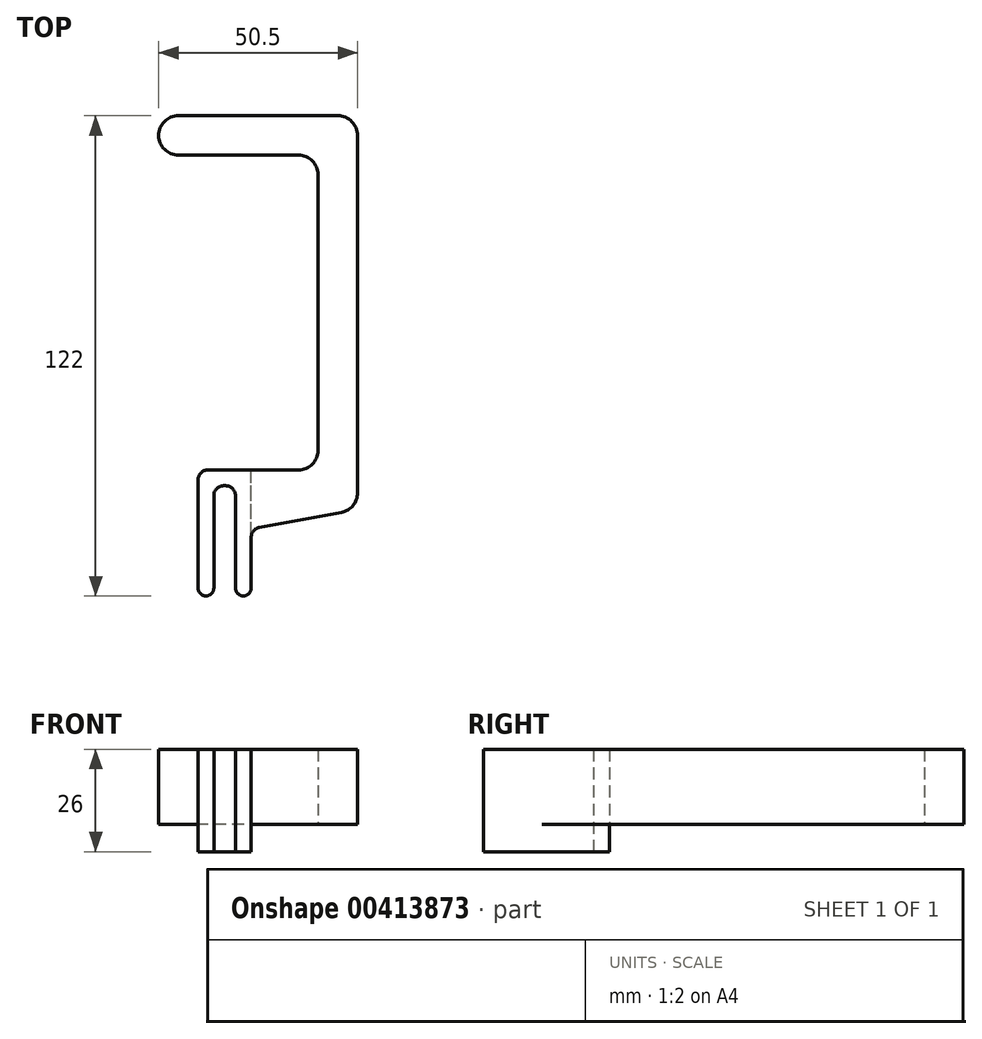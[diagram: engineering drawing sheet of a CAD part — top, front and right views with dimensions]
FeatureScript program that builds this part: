
annotation { "Feature Type Name" : "Feature", "Feature Type Description" : "" }
export const myFeature = defineFeature(function(context is Context, id is Id, definition is map)
    precondition{}
    {
        {
            var Q0;
            Q0=qCreatedBy(makeId("Top.planeOp"),FACE);
            var sketch = newSketch(context, id + "F0", { "sketchPlane" : qUnion([Q0])});
            skLineSegment(sketch, "E0", {"start": v(0, 0) * mm, "end": v(0, 30) * mm});
            skLineSegment(sketch, "E1", {"start": v(0, 0) * mm, "end": v(4, 0) * mm});
            skLineSegment(sketch, "E2", {"start": v(4, 0) * mm, "end": v(4, 26) * mm});
            skLineSegment(sketch, "E3", {"start": v(4, 26) * mm, "end": v(9.5, 26) * mm});
            skLineSegment(sketch, "E4", {"start": v(9.5, 26) * mm, "end": v(9.5, 0) * mm});
            skLineSegment(sketch, "E5", {"start": v(0, 30) * mm, "end": v(30.5, 30) * mm});
            skLineSegment(sketch, "E6", {"start": v(30.5, 30) * mm, "end": v(30.5, 110) * mm});
            skLineSegment(sketch, "E7", {"start": v(30.5, 120) * mm, "end": v(40.5, 120) * mm});
            skLineSegment(sketch, "E8", {"start": v(40.5, 120) * mm, "end": v(40.5, 20) * mm});
            skArc(sketch, "E9", {"start": v(0, 0) * mm, "mid": v(2, -2) * mm, "end": v(4, 0) * mm});
            skLineSegment(sketch, "E10", {"start": v(9.5, 0) * mm, "end": v(13.5, 0) * mm});
            skLineSegment(sketch, "E11", {"start": v(13.5, 0) * mm, "end": v(13.5, 15) * mm});
            skArc(sketch, "E12", {"start": v(9.5, 0) * mm, "mid": v(11.5, -2) * mm, "end": v(13.5, 0) * mm});
            skLineSegment(sketch, "E13.bottom", {"start": v(30.5, 120) * mm, "end": v(-5, 120) * mm});
            skLineSegment(sketch, "E13.top", {"start": v(30.5, 110) * mm, "end": v(-5, 110) * mm});
            skLineSegment(sketch, "E13.right", {"start": v(-5, 120) * mm, "end": v(-5, 110) * mm});
            skArc(sketch, "E14", {"start": v(-5, 120) * mm, "mid": v(-10, 115) * mm, "end": v(-5, 110) * mm});
            skLineSegment(sketch, "E15", {"start": v(13.5, 15) * mm, "end": v(40.5, 20) * mm});
            skPoint(sketch, "E16.end.orphan", {"position": v(40.5, 15) * mm});
            skSolve(sketch);
        }
        {
            var Q0;
            Q0 = qSketchRegion(id + "F0", true);
            extrude(context, id + "F1", {"entities" : qUnion([Q0]), "depth" : 26 * mm});
        }
        {
            var Q0;
            Q0=makeQuery(id+"F1.opExtrude","CAP_FACE",FACE,{"disambiguationData":[OSD([sQuery(id+"F0.wireOp",EDGE,"E0"),sQuery(id+"F0.wireOp",EDGE,"E2"),sQuery(id+"F0.wireOp",EDGE,"E3"),sQuery(id+"F0.wireOp",EDGE,"E4"),sQuery(id+"F0.wireOp",EDGE,"E5"),sQuery(id+"F0.wireOp",EDGE,"E6"),sQuery(id+"F0.wireOp",EDGE,"E7"),sQuery(id+"F0.wireOp",EDGE,"E8"),sQuery(id+"F0.wireOp",EDGE,"E9"),sQuery(id+"F0.wireOp",EDGE,"E11"),sQuery(id+"F0.wireOp",EDGE,"E12"),sQuery(id+"F0.wireOp",EDGE,"E16")])],"isStart":true});
            var sketch = newSketch(context, id + "F2", { "sketchPlane" : qUnion([Q0])});
            skLineSegment(sketch, "E17.0", {"start": v(40.5, -120) * mm, "end": v(40.5, -120) * mm});
            skLineSegment(sketch, "E17.1", {"start": v(40.5, -120) * mm, "end": v(40.5, -120) * mm});
            skLineSegment(sketch, "E17.2", {"start": v(30.5, -30) * mm, "end": v(30.5, -110) * mm});
            skLineSegment(sketch, "E17.3", {"start": v(0, -30) * mm, "end": v(30.5, -30) * mm});
            skLineSegment(sketch, "E17.4", {"start": v(13.5, -120) * mm, "end": v(40.5, -120) * mm});
            skPoint(sketch, "E17.5", {"position": v(17.75, -120) * mm});
            skLineSegment(sketch, "E18.0", {"start": v(30.5, -110) * mm, "end": v(-5, -110) * mm});
            skArc(sketch, "E18.1", {"start": v(-5, -120) * mm, "mid": v(-10, -115) * mm, "end": v(-5, -110) * mm});
            skLineSegment(sketch, "E18.2", {"start": v(-5, -120) * mm, "end": v(40.5, -120) * mm});
            skLineSegment(sketch, "E19.0", {"start": v(40.5, -120) * mm, "end": v(40.5, -20) * mm});
            skLineSegment(sketch, "E19.1", {"start": v(13.5, -15) * mm, "end": v(40.5, -20) * mm});
            skLineSegment(sketch, "E20", {"start": v(13.5, -15) * mm, "end": v(13.5, -30) * mm});
            skSolve(sketch);
        }
        {
            var Q0;
            Q0 = qSketchRegion(id + "F2", true);
            extrude(context, id + "F3", {"entities" : qUnion([Q0]), "operationType" : NewBodyOperationType.REMOVE, "oppositeDirection" : true, "depth" : 7 * mm});
        }
        {
            var Q0;
            Q0=makeQuery(id+"F1.opExtrude","SWEPT_EDGE",EDGE,{"disambiguationData":[OSD([sQuery(id+"F0.wireOp",EDGE,"E7"),sQuery(id+"F0.wireOp",EDGE,"E8")])]});
            var Q1;
            Q1=makeQuery(id+"F1.opExtrude","SWEPT_EDGE",EDGE,{"disambiguationData":[OSD([sQuery(id+"F0.wireOp",EDGE,"E6"),sQuery(id+"F0.wireOp",EDGE,"E13.top")])]});
            var Q2;
            Q2=makeQuery(id+"F1.opExtrude","SWEPT_EDGE",EDGE,{"disambiguationData":[OSD([sQuery(id+"F0.wireOp",EDGE,"E5"),sQuery(id+"F0.wireOp",EDGE,"E6")])]});
            var Q3;
            Q3=makeQuery(id+"F1.opExtrude","SWEPT_EDGE",EDGE,{"disambiguationData":[OSD([sQuery(id+"F0.wireOp",EDGE,"E8"),sQuery(id+"F0.wireOp",EDGE,"E16")])]});
            fillet(context, id + "F4", {"entities" : qUnion([Q0, Q1, Q2, Q3]), "radius" : 5 * mm, "tangentPropagation" : true, "allowEdgeOverflow" : false});
        }
        {
            var Q0;
            Q0=makeQuery(id+"F1.opExtrude","SWEPT_EDGE",EDGE,{"disambiguationData":[OSD([sQuery(id+"F0.wireOp",EDGE,"E0"),sQuery(id+"F0.wireOp",EDGE,"E5")])]});
            var Q1;
            Q1=makeQuery(id+"F1.opExtrude","SWEPT_EDGE",EDGE,{"disambiguationData":[OSD([sQuery(id+"F0.wireOp",EDGE,"E2"),sQuery(id+"F0.wireOp",EDGE,"E3")])]});
            var Q2;
            Q2=makeQuery(id+"F1.opExtrude","SWEPT_EDGE",EDGE,{"disambiguationData":[OSD([sQuery(id+"F0.wireOp",EDGE,"E3"),sQuery(id+"F0.wireOp",EDGE,"E4")])]});
            var Q3;
            Q3=makeQuery(id+"F1.opExtrude","SWEPT_EDGE",EDGE,{"disambiguationData":[OSD([sQuery(id+"F0.wireOp",EDGE,"E11"),sQuery(id+"F0.wireOp",EDGE,"E16")])]});
            var Q4;
            Q4=makeQuery(id+"F3.boolean.opBoolean","COPY",EDGE,{"derivedFrom":makeQuery(id+"F3.opExtrude","SWEPT_EDGE",EDGE,{"disambiguationData":[OSD([sQuery(id+"F2.wireOp",EDGE,"E17.3"),sQuery(id+"F2.wireOp",EDGE,"fISdSf13-6yRy-rc2g-W1Nq-7AvC3r0ghYyL")])]})});
            fillet(context, id + "F5", {"entities" : qUnion([Q0, Q1, Q2, Q3, Q4]), "radius" : 2.5 * mm, "tangentPropagation" : true, "allowEdgeOverflow" : false});
        }
    });
